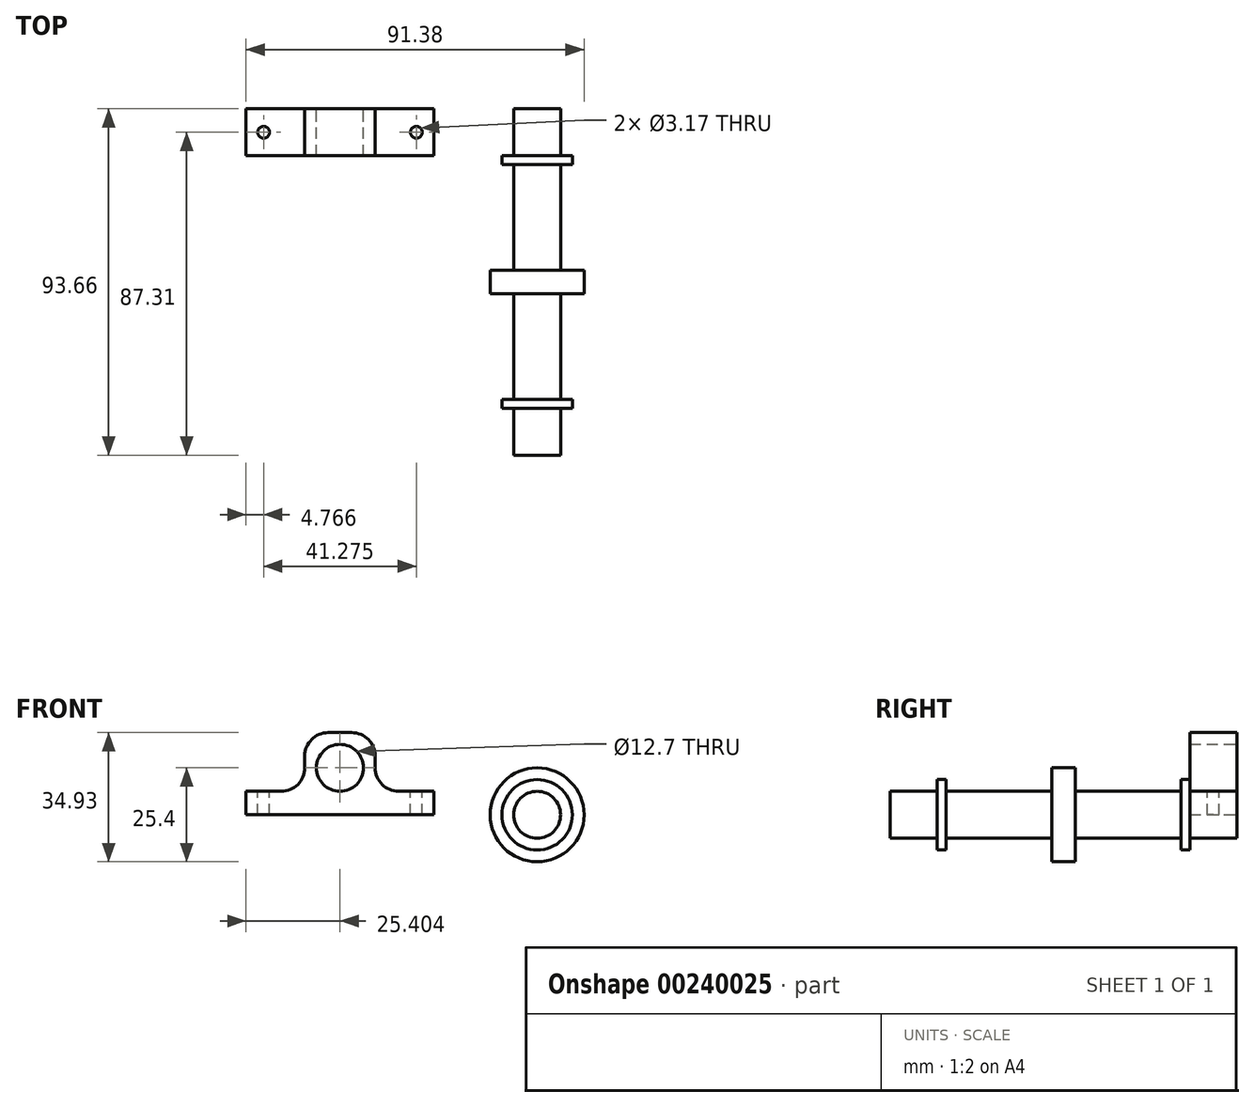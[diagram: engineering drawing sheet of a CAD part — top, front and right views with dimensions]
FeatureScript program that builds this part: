
annotation { "Feature Type Name" : "Feature", "Feature Type Description" : "" }
export const myFeature = defineFeature(function(context is Context, id is Id, definition is map)
    precondition{}
    {
        {
            var Q0;
            Q0=qCreatedBy(makeId("Front.planeOp"),FACE);
            var sketch = newSketch(context, id + "F0", { "sketchPlane" : qUnion([Q0])});
            skCircle(sketch, "E0", {"center": v(0, 0) * mm, "radius": 6.35 * mm});
            skSolve(sketch);
        }
        {
            var Q0;
            Q0=makeQuery(id+"F0.imprint","IMPRINT",FACE,{"disambiguationData":[TD([[makeQuery(id+"F0.imprint","IMPRINT",EDGE,{"derivedFrom":sQuery(id+"F0.wireOp",EDGE,"E0")}),1.0]])]});
            extrude(context, id + "F1", {"entities" : qUnion([Q0]), "depth" : 12.7 * mm});
        }
        {
            var Q0;
            Q0=makeQuery(id+"F1.opExtrude","CAP_FACE",FACE,{"disambiguationData":[OSD([sQuery(id+"F0.wireOp",EDGE,"E0")])],"isStart":false});
            var sketch = newSketch(context, id + "F2", { "sketchPlane" : qUnion([Q0])});
            skCircle(sketch, "E1", {"center": v(0, 0) * mm, "radius": 9.52 * mm});
            skSolve(sketch);
        }
        {
            var Q0;
            Q0=makeQuery(id+"F2.imprint","IMPRINT",FACE,{"disambiguationData":[TD([[makeQuery(id+"F2.imprint","IMPRINT",EDGE,{"derivedFrom":makeQuery(id+"F1.opExtrude","CAP_EDGE",EDGE,{"disambiguationData":[OSD([sQuery(id+"F0.wireOp",EDGE,"E0")])],"isStart":false})}),1.0]])]});
            var Q1;
            Q1=makeQuery(id+"F2.imprint","IMPRINT",FACE,{"disambiguationData":[TD([[makeQuery(id+"F2.imprint","IMPRINT",EDGE,{"derivedFrom":sQuery(id+"F2.wireOp",EDGE,"E1")}),1.0]])]});
            extrude(context, id + "F3", {"entities" : qUnion([Q0, Q1]), "operationType" : NewBodyOperationType.ADD, "depth" : 2.38 * mm});
        }
        {
            var Q0;
            Q0=makeQuery(id+"F3.opExtrude","CAP_FACE",FACE,{"disambiguationData":[OSD([sQuery(id+"F2.wireOp",EDGE,"E1")])],"isStart":false});
            var sketch = newSketch(context, id + "F4", { "sketchPlane" : qUnion([Q0])});
            skCircle(sketch, "E2", {"center": v(0, 0) * mm, "radius": 6.35 * mm});
            skSolve(sketch);
        }
        {
            var Q0;
            Q0=makeQuery(id+"F4.imprint","IMPRINT",FACE,{"disambiguationData":[TD([[makeQuery(id+"F4.imprint","IMPRINT",EDGE,{"derivedFrom":sQuery(id+"F4.wireOp",EDGE,"E2")}),1.0]])]});
            extrude(context, id + "F5", {"entities" : qUnion([Q0]), "operationType" : NewBodyOperationType.ADD, "depth" : 28.57 * mm});
        }
        {
            var Q0;
            Q0=makeQuery(id+"F5.opExtrude","CAP_FACE",FACE,{"disambiguationData":[OSD([sQuery(id+"F4.wireOp",EDGE,"E2")])],"isStart":false});
            var sketch = newSketch(context, id + "F6", { "sketchPlane" : qUnion([Q0])});
            skCircle(sketch, "E3", {"center": v(0, 0) * mm, "radius": 12.7 * mm});
            skSolve(sketch);
        }
        {
            var Q0;
            Q0=makeQuery(id+"F6.imprint","IMPRINT",FACE,{"disambiguationData":[TD([[makeQuery(id+"F6.imprint","IMPRINT",EDGE,{"derivedFrom":makeQuery(id+"F5.opExtrude","CAP_EDGE",EDGE,{"disambiguationData":[OSD([sQuery(id+"F4.wireOp",EDGE,"E2")])],"isStart":false})}),1.0]])]});
            var Q1;
            Q1=makeQuery(id+"F6.imprint","IMPRINT",FACE,{"disambiguationData":[TD([[makeQuery(id+"F6.imprint","IMPRINT",EDGE,{"derivedFrom":sQuery(id+"F6.wireOp",EDGE,"E3")}),1.0]])]});
            extrude(context, id + "F7", {"entities" : qUnion([Q0, Q1]), "operationType" : NewBodyOperationType.ADD, "depth" : 6.35 * mm});
        }
        {
            var Q0;
            Q0=makeQuery(id+"F7.opExtrude","CAP_FACE",FACE,{"disambiguationData":[OSD([sQuery(id+"F6.wireOp",EDGE,"E3")])],"isStart":false});
            var sketch = newSketch(context, id + "F8", { "sketchPlane" : qUnion([Q0])});
            skCircle(sketch, "E4", {"center": v(0, 0) * mm, "radius": 6.35 * mm});
            skSolve(sketch);
        }
        {
            var Q0;
            Q0=makeQuery(id+"F8.imprint","IMPRINT",FACE,{"disambiguationData":[TD([[makeQuery(id+"F8.imprint","IMPRINT",EDGE,{"derivedFrom":sQuery(id+"F8.wireOp",EDGE,"E4")}),1.0]])]});
            extrude(context, id + "F9", {"entities" : qUnion([Q0]), "operationType" : NewBodyOperationType.ADD, "depth" : 28.57 * mm});
        }
        {
            var Q0;
            Q0=makeQuery(id+"F9.opExtrude","CAP_FACE",FACE,{"disambiguationData":[OSD([sQuery(id+"F8.wireOp",EDGE,"E4")])],"isStart":false});
            var sketch = newSketch(context, id + "F10", { "sketchPlane" : qUnion([Q0])});
            skCircle(sketch, "E5", {"center": v(0, 0) * mm, "radius": 9.53 * mm});
            skSolve(sketch);
        }
        {
            var Q0;
            Q0=makeQuery(id+"F10.imprint","IMPRINT",FACE,{"disambiguationData":[TD([[makeQuery(id+"F10.imprint","IMPRINT",EDGE,{"derivedFrom":makeQuery(id+"F9.opExtrude","CAP_EDGE",EDGE,{"disambiguationData":[OSD([sQuery(id+"F8.wireOp",EDGE,"E4")])],"isStart":false})}),1.0]])]});
            var Q1;
            Q1=makeQuery(id+"F10.imprint","IMPRINT",FACE,{"disambiguationData":[TD([[makeQuery(id+"F10.imprint","IMPRINT",EDGE,{"derivedFrom":sQuery(id+"F10.wireOp",EDGE,"E5")}),1.0]])]});
            extrude(context, id + "F11", {"entities" : qUnion([Q0, Q1]), "operationType" : NewBodyOperationType.ADD, "depth" : 2.38 * mm});
        }
        {
            var Q0;
            Q0=makeQuery(id+"F11.opExtrude","CAP_FACE",FACE,{"disambiguationData":[OSD([sQuery(id+"F10.wireOp",EDGE,"E5")])],"isStart":false});
            var sketch = newSketch(context, id + "F12", { "sketchPlane" : qUnion([Q0])});
            skCircle(sketch, "E6", {"center": v(0, 0) * mm, "radius": 6.35 * mm});
            skSolve(sketch);
        }
        {
            var Q0;
            Q0=makeQuery(id+"F12.imprint","IMPRINT",FACE,{"disambiguationData":[TD([[makeQuery(id+"F12.imprint","IMPRINT",EDGE,{"derivedFrom":sQuery(id+"F12.wireOp",EDGE,"E6")}),1.0]])]});
            extrude(context, id + "F13", {"entities" : qUnion([Q0]), "operationType" : NewBodyOperationType.ADD, "depth" : 12.7 * mm});
        }
        {
            var Q0;
            Q0=qCreatedBy(makeId("Front.planeOp"),FACE);
            var sketch = newSketch(context, id + "F14", { "sketchPlane" : qUnion([Q0])});
            skLineSegment(sketch, "E7.bottom", {"start": v(-27.88, 0) * mm, "end": v(-78.68, 0) * mm});
            skLineSegment(sketch, "E7.top", {"start": v(-27.88, 25.4) * mm, "end": v(-43.75, 25.4) * mm});
            skLineSegment(sketch, "E7.left", {"start": v(-27.88, 0) * mm, "end": v(-27.88, 25.4) * mm});
            skLineSegment(sketch, "E7.right", {"start": v(-78.68, 0) * mm, "end": v(-78.68, 25.4) * mm});
            skLineSegment(sketch, "E8.bottom", {"start": v(-78.68, 25.4) * mm, "end": v(-62.8, 25.4) * mm});
            skLineSegment(sketch, "E8.top", {"start": v(-78.68, 6.35) * mm, "end": v(-62.8, 6.35) * mm});
            skLineSegment(sketch, "E8.left", {"start": v(-78.68, 25.4) * mm, "end": v(-78.68, 6.35) * mm});
            skLineSegment(sketch, "E8.right", {"start": v(-62.8, 22.23) * mm, "end": v(-62.8, 6.35) * mm});
            skCircle(sketch, "E9", {"center": v(-53.28, 12.7) * mm, "radius": 6.35 * mm});
            skPoint(sketch, "E9.centerSnap0", {"position": v(-53.28, 0) * mm});
            skPoint(sketch, "E9.centerSnap1", {"position": v(-27.88, 12.7) * mm});
            skPoint(sketch, "E10.oppositeSnap0", {"position": v(-70.74, 6.35) * mm});
            skLineSegment(sketch, "E10.top", {"start": v(-27.88, 6.35) * mm, "end": v(-43.75, 6.35) * mm});
            skLineSegment(sketch, "E10.left", {"start": v(-27.88, 25.4) * mm, "end": v(-27.88, 6.35) * mm});
            skLineSegment(sketch, "E10.right", {"start": v(-43.75, 22.23) * mm, "end": v(-43.75, 6.35) * mm});
            skLineSegment(sketch, "E11.bottom", {"start": v(-43.75, 25.4) * mm, "end": v(-62.8, 25.4) * mm});
            skLineSegment(sketch, "E11.top", {"start": v(-43.75, 22.23) * mm, "end": v(-62.8, 22.23) * mm});
            skLineSegment(sketch, "E11.left", {"start": v(-43.75, 25.4) * mm, "end": v(-43.75, 22.23) * mm});
            skLineSegment(sketch, "E11.right", {"start": v(-62.8, 25.4) * mm, "end": v(-62.8, 22.23) * mm});
            skLineSegment(sketch, "E12.trimOffspring", {"start": v(-62.8, 25.4) * mm, "end": v(-78.68, 25.4) * mm});
            skSolve(sketch);
        }
        {
            var Q0;
            Q0=makeQuery(id+"F14.imprint","IMPRINT",FACE,{"disambiguationData":[TD([[makeQuery(id+"F14.imprint","IMPRINT",EDGE,{"derivedFrom":sQuery(id+"F14.wireOp",EDGE,"E7.bottom")}),-1.0]])]});
            extrude(context, id + "F15", {"entities" : qUnion([Q0]), "depth" : 12.7 * mm});
        }
        {
            var Q0;
            Q0=makeQuery(id+"F15.opExtrude","SWEPT_EDGE",EDGE,{"disambiguationData":[OSD([sQuery(id+"F14.wireOp",EDGE,"E10.top"),sQuery(id+"F14.wireOp",EDGE,"E10.right")])]});
            var Q1;
            Q1=makeQuery(id+"F15.opExtrude","SWEPT_EDGE",EDGE,{"disambiguationData":[OSD([sQuery(id+"F14.wireOp",EDGE,"E10.right"),sQuery(id+"F14.wireOp",EDGE,"E11.top"),sQuery(id+"F14.wireOp",EDGE,"E11.left")])]});
            var Q2;
            Q2=makeQuery(id+"F15.opExtrude","SWEPT_EDGE",EDGE,{"disambiguationData":[OSD([sQuery(id+"F14.wireOp",EDGE,"E8.right"),sQuery(id+"F14.wireOp",EDGE,"E11.top"),sQuery(id+"F14.wireOp",EDGE,"E11.right")])]});
            var Q3;
            Q3=makeQuery(id+"F15.opExtrude","SWEPT_EDGE",EDGE,{"disambiguationData":[OSD([sQuery(id+"F14.wireOp",EDGE,"E8.top"),sQuery(id+"F14.wireOp",EDGE,"E8.right")])]});
            fillet(context, id + "F16", {"entities" : qUnion([Q0, Q1, Q2, Q3]), "radius" : 6.35 * mm, "tangentPropagation" : true, "allowEdgeOverflow" : false});
        }
        {
            var Q0;
            Q0=makeQuery(id+"F15.opExtrude","SWEPT_FACE",FACE,{"disambiguationData":[OSD([sQuery(id+"F14.wireOp",EDGE,"E8.top")])]});
            var sketch = newSketch(context, id + "F17", { "sketchPlane" : qUnion([Q0])});
            skCircle(sketch, "E13", {"center": v(-73.91, -6.35) * mm, "radius": 1.59 * mm});
            skPoint(sketch, "E13.centerSnap0", {"position": v(-73.91, 0) * mm});
            skPoint(sketch, "E13.centerSnap1", {"position": v(-78.68, -6.35) * mm});
            skCircle(sketch, "E14", {"center": v(-32.64, -6.35) * mm, "radius": 1.59 * mm});
            skSolve(sketch);
        }
        {
            var Q0;
            Q0 = qSketchRegion(id + "F17", true);
            extrude(context, id + "F18", {"entities" : qUnion([Q0]), "operationType" : NewBodyOperationType.REMOVE, "endBound" : BoundingType.UP_TO_NEXT, "oppositeDirection" : true, "depth" : 25.4 * mm});
        }
    });
